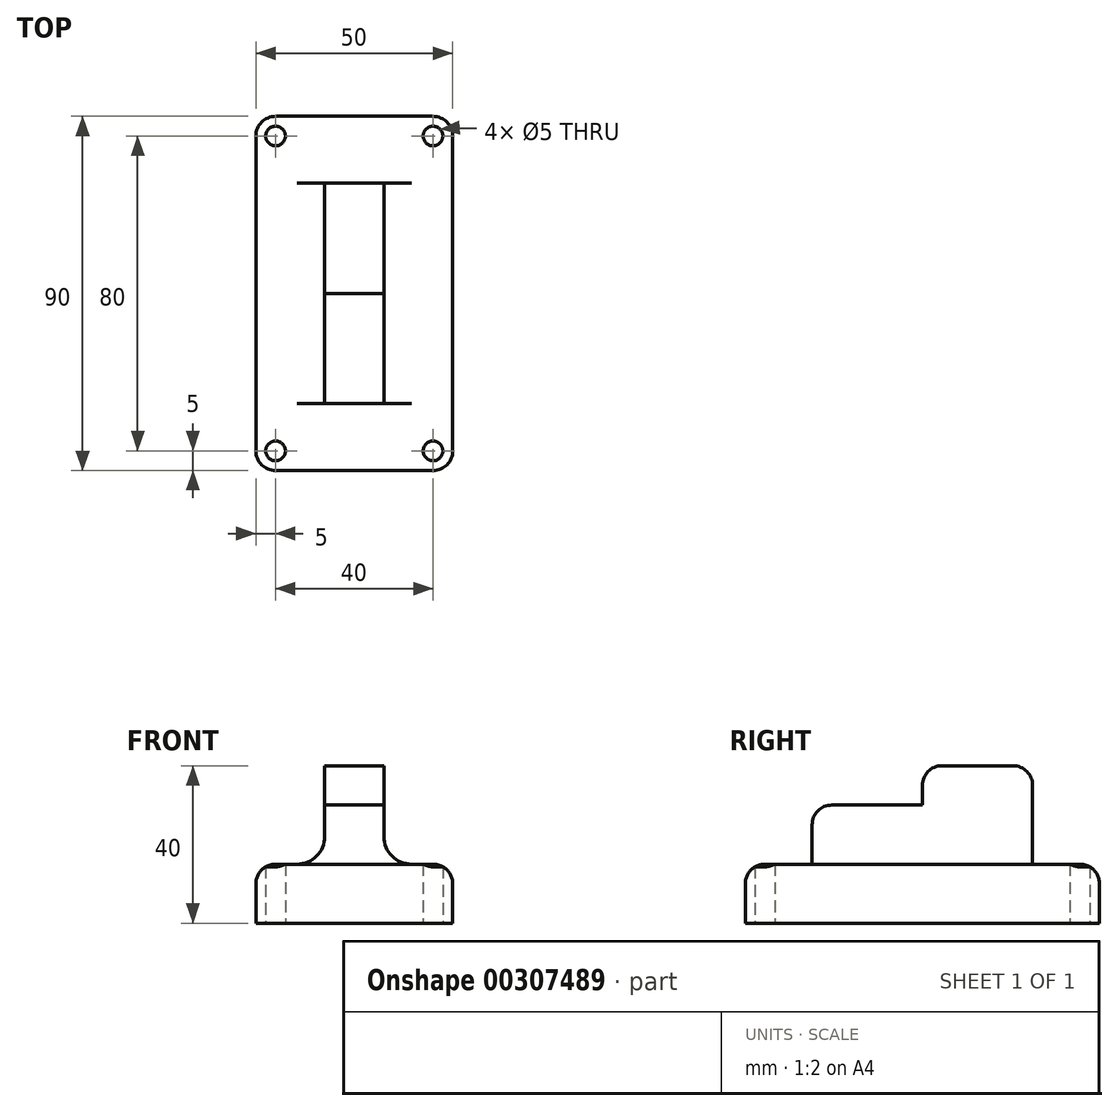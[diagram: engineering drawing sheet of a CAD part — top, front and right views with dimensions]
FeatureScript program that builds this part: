
annotation { "Feature Type Name" : "Feature", "Feature Type Description" : "" }
export const myFeature = defineFeature(function(context is Context, id is Id, definition is map)
    precondition{}
    {
        {
            var Q0;
            Q0=qCreatedBy(makeId("Top.planeOp"),FACE);
            var sketch = newSketch(context, id + "F0", { "sketchPlane" : qUnion([Q0])});
            skLineSegment(sketch, "E0.bottom", {"start": v(-20, -45) * mm, "end": v(20, -45) * mm});
            skLineSegment(sketch, "E0.top", {"start": v(-20, 45) * mm, "end": v(20, 45) * mm});
            skLineSegment(sketch, "E0.left", {"start": v(-25, -40) * mm, "end": v(-25, 40) * mm});
            skLineSegment(sketch, "E0.right", {"start": v(25, -40) * mm, "end": v(25, 40) * mm});
            skPoint(sketch, "E0.middle", {"position": v(0, 0) * mm});
            skPoint(sketch, "E1.visualSharp", {"position": v(-25, 45) * mm});
            skArc(sketch, "E1.filletArc", {"start": v(-20, 45) * mm, "mid": v(-23.54, 43.54) * mm, "end": v(-25, 40) * mm});
            skPoint(sketch, "E2.visualSharp", {"position": v(25, 45) * mm});
            skArc(sketch, "E2.filletArc", {"start": v(25, 40) * mm, "mid": v(23.54, 43.54) * mm, "end": v(20, 45) * mm});
            skPoint(sketch, "E3.visualSharp", {"position": v(25, -45) * mm});
            skArc(sketch, "E3.filletArc", {"start": v(20, -45) * mm, "mid": v(23.54, -43.54) * mm, "end": v(25, -40) * mm});
            skPoint(sketch, "E4.visualSharp", {"position": v(-25, -45) * mm});
            skArc(sketch, "E4.filletArc", {"start": v(-25, -40) * mm, "mid": v(-23.54, -43.54) * mm, "end": v(-20, -45) * mm});
            skCircle(sketch, "E5", {"center": v(20, 40) * mm, "radius": 2.5 * mm});
            skCircle(sketch, "E6", {"center": v(-20, 40) * mm, "radius": 2.5 * mm});
            skCircle(sketch, "E7", {"center": v(-20, -40) * mm, "radius": 2.5 * mm});
            skCircle(sketch, "E8", {"center": v(20, -40) * mm, "radius": 2.5 * mm});
            skLineSegment(sketch, "E9.bottom", {"start": v(-7.5, -28) * mm, "end": v(7.5, -28) * mm, "construction": true});
            skLineSegment(sketch, "E9.top", {"start": v(-7.5, 28) * mm, "end": v(7.5, 28) * mm, "construction": true});
            skLineSegment(sketch, "E9.left", {"start": v(-7.5, -28) * mm, "end": v(-7.5, 28) * mm, "construction": true});
            skLineSegment(sketch, "E9.right", {"start": v(7.5, -28) * mm, "end": v(7.5, 28) * mm, "construction": true});
            skLineSegment(sketch, "E10", {"start": v(7.5, 0) * mm, "end": v(-7.5, 0) * mm});
            skLineSegment(sketch, "E11.bottom", {"start": v(-7.5, -28) * mm, "end": v(7.5, -28) * mm});
            skLineSegment(sketch, "E11.top", {"start": v(-7.5, 28) * mm, "end": v(7.5, 28) * mm});
            skLineSegment(sketch, "E11.left", {"start": v(-7.5, -28) * mm, "end": v(-7.5, 28) * mm});
            skLineSegment(sketch, "E11.right", {"start": v(7.5, -28) * mm, "end": v(7.5, 28) * mm});
            skSolve(sketch);
        }
        {
            var Q0;
            Q0=makeQuery(id+"F0.imprint","IMPRINT",FACE,{"disambiguationData":[TD([[makeQuery(id+"F0.imprint","IMPRINT",EDGE,{"derivedFrom":sQuery(id+"F0.wireOp",EDGE,"E0.bottom")}),1.0]])]});
            extrude(context, id + "F1", {"entities" : qUnion([Q0]), "depth" : 15 * mm});
        }
        {
            var Q0;
            {var subQ0=sQuery(id+"F0.wireOp",EDGE,"E10");Q0=makeQuery(id+"F0.imprint","IMPRINT",FACE,{"disambiguationData":[TD([[makeQuery(id+"F0.imprint","IMPRINT",EDGE,{"derivedFrom":subQ0}),-1.0]])]});}
            extrude(context, id + "F2", {"entities" : qUnion([Q0]), "operationType" : NewBodyOperationType.ADD, "depth" : 40 * mm});
        }
        {
            var Q0;
            {var subQ0=sQuery(id+"F0.wireOp",EDGE,"E10");Q0=makeQuery(id+"F0.imprint","IMPRINT",FACE,{"disambiguationData":[TD([[makeQuery(id+"F0.imprint","IMPRINT",EDGE,{"derivedFrom":subQ0}),1.0]])]});}
            extrude(context, id + "F3", {"entities" : qUnion([Q0]), "operationType" : NewBodyOperationType.ADD, "depth" : 30 * mm});
        }
        {
            var Q0;
            Q0=makeQuery(id+"F2.opExtrude","CAP_EDGE",EDGE,{"disambiguationData":[OSD([sQuery(id+"F0.wireOp",EDGE,"E10")])],"isStart":false});
            var Q1;
            Q1=makeQuery(id+"F2.opExtrude","CAP_EDGE",EDGE,{"disambiguationData":[OSD([sQuery(id+"F0.wireOp",EDGE,"E11.top")])],"isStart":false});
            var Q2;
            Q2=makeQuery(id+"F3.opExtrude","CAP_EDGE",EDGE,{"disambiguationData":[OSD([sQuery(id+"F0.wireOp",EDGE,"E10")])],"isStart":false});
            var Q3;
            Q3=makeQuery(id+"F1.opExtrude","CAP_EDGE",EDGE,{"disambiguationData":[OSD([sQuery(id+"F0.wireOp",EDGE,"E0.bottom")])],"isStart":false});
            var Q4;
            Q4=makeQuery(id+"F1.opExtrude","CAP_EDGE",EDGE,{"disambiguationData":[OSD([sQuery(id+"F0.wireOp",EDGE,"E4.filletArc")])],"isStart":false});
            var Q5;
            Q5=makeQuery(id+"F3.opExtrude","CAP_EDGE",EDGE,{"disambiguationData":[OSD([sQuery(id+"F0.wireOp",EDGE,"E11.bottom")])],"isStart":false});
            fillet(context, id + "F4", {"entities" : qUnion([Q0, Q1, Q2, Q3, Q4, Q5]), "radius" : 5 * mm, "tangentPropagation" : true, "allowEdgeOverflow" : false});
        }
        {
            var Q0;
            {var subQ0=sQuery(id+"F0.wireOp",EDGE,"E11.left");var subQ2=makeQuery(id+"F1.opExtrude","CAP_EDGE",EDGE,{"disambiguationData":[OSD([subQ0])],"isStart":false});Q0=makeQuery(id+"F3.boolean.opBoolean","MERGE",EDGE,{"derivedFrom":[makeQuery(id+"F2.boolean.opBoolean","SPLIT",EDGE,{"disambiguationData":[topologyDisambiguationEdgeConnected([makeQuery(id+"F1.opExtrude","SWEPT_FACE",FACE,{"disambiguationData":[OSD([subQ0])]})])],"derivedFrom":subQ2}),makeQuery(id+"F2.boolean.opBoolean","SPLIT",EDGE,{"disambiguationData":[topologyDisambiguationEdgeConnected([makeQuery(id+"F2.opExtrude","SWEPT_FACE",FACE,{"disambiguationData":[OSD([subQ0])]})])],"derivedFrom":subQ2})]});}
            var Q1;
            {var subQ0=sQuery(id+"F0.wireOp",EDGE,"E11.right");var subQ2=makeQuery(id+"F1.opExtrude","CAP_EDGE",EDGE,{"disambiguationData":[OSD([subQ0])],"isStart":false});Q1=makeQuery(id+"F3.boolean.opBoolean","MERGE",EDGE,{"derivedFrom":[makeQuery(id+"F2.boolean.opBoolean","SPLIT",EDGE,{"disambiguationData":[topologyDisambiguationEdgeConnected([makeQuery(id+"F1.opExtrude","SWEPT_FACE",FACE,{"disambiguationData":[OSD([subQ0])]})])],"derivedFrom":subQ2}),makeQuery(id+"F2.boolean.opBoolean","SPLIT",EDGE,{"disambiguationData":[topologyDisambiguationEdgeConnected([makeQuery(id+"F2.opExtrude","SWEPT_FACE",FACE,{"disambiguationData":[OSD([subQ0])]})])],"derivedFrom":subQ2})]});}
            fillet(context, id + "F5", {"entities" : qUnion([Q0, Q1]), "radius" : 7 * mm, "tangentPropagation" : true, "allowEdgeOverflow" : false});
        }
    });
